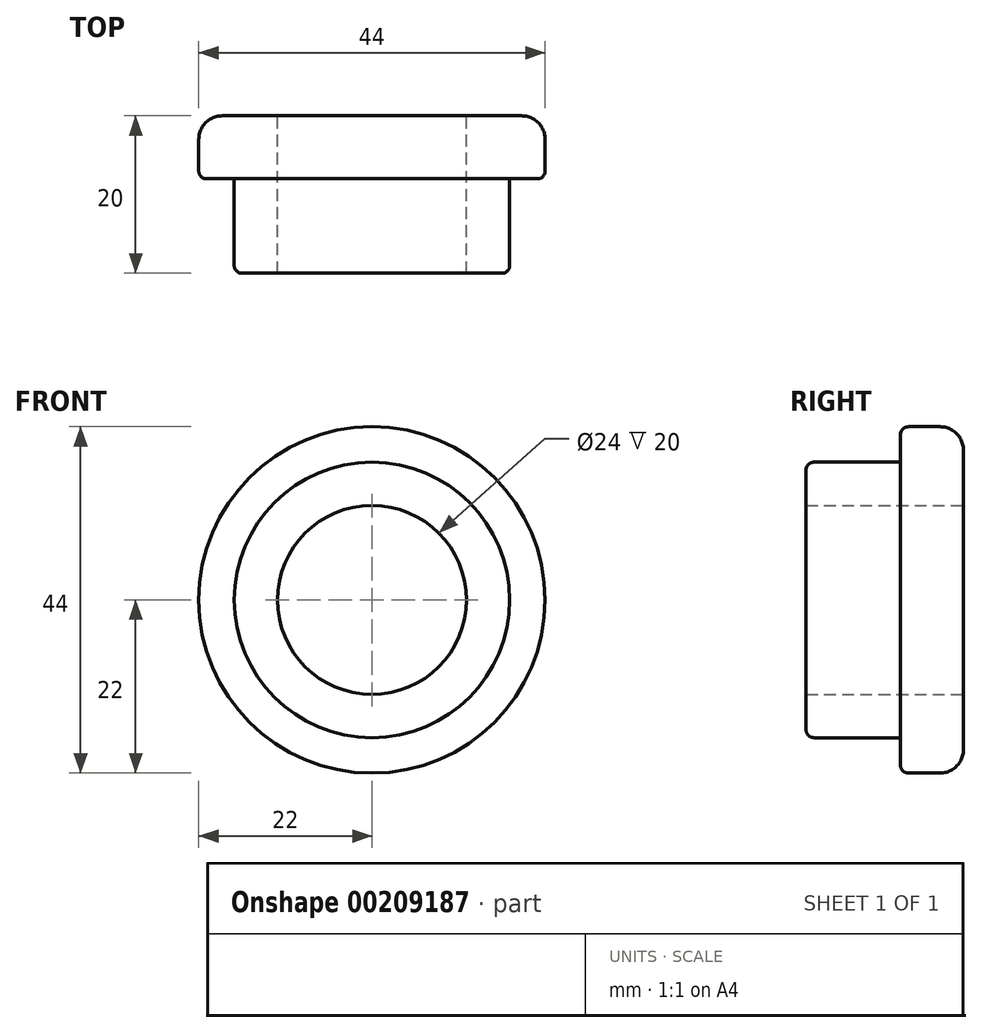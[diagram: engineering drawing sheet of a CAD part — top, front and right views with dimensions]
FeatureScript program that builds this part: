
annotation { "Feature Type Name" : "Feature", "Feature Type Description" : "" }
export const myFeature = defineFeature(function(context is Context, id is Id, definition is map)
    precondition{}
    {
        {
            var Q0;
            Q0=qCreatedBy(makeId("Front.planeOp"),FACE);
            var sketch = newSketch(context, id + "F0", { "sketchPlane" : qUnion([Q0])});
            skCircle(sketch, "E0", {"center": v(0, 0) * mm, "radius": 17.5 * mm});
            skCircle(sketch, "E1", {"center": v(0, 0) * mm, "radius": 22 * mm});
            skCircle(sketch, "E2", {"center": v(0, 0) * mm, "radius": 12 * mm});
            skSolve(sketch);
        }
        {
            var Q0;
            Q0=makeQuery(id+"F0.imprint","IMPRINT",FACE,{"disambiguationData":[TD([[makeQuery(id+"F0.imprint","IMPRINT",EDGE,{"derivedFrom":sQuery(id+"F0.wireOp",EDGE,"E0")}),-1.0]])]});
            var Q1;
            Q1=makeQuery(id+"F0.imprint","IMPRINT",FACE,{"disambiguationData":[TD([[makeQuery(id+"F0.imprint","IMPRINT",EDGE,{"derivedFrom":sQuery(id+"F0.wireOp",EDGE,"E0")}),1.0]])]});
            extrude(context, id + "F1", {"entities" : qUnion([Q0, Q1]), "depth" : 8 * mm});
        }
        {
            var Q0;
            Q0=makeQuery(id+"F0.imprint","IMPRINT",FACE,{"disambiguationData":[TD([[makeQuery(id+"F0.imprint","IMPRINT",EDGE,{"derivedFrom":sQuery(id+"F0.wireOp",EDGE,"E0")}),1.0]])]});
            extrude(context, id + "F2", {"entities" : qUnion([Q0]), "operationType" : NewBodyOperationType.ADD, "depth" : 20 * mm});
        }
        {
            var Q0;
            Q0=makeQuery(id+"F1.opExtrude","CAP_EDGE",EDGE,{"disambiguationData":[OSD([sQuery(id+"F0.wireOp",EDGE,"E1")])],"isStart":true});
            fillet(context, id + "F3", {"entities" : qUnion([Q0]), "radius" : 3 * mm, "tangentPropagation" : true, "allowEdgeOverflow" : false});
        }
        {
            var Q0;
            Q0=makeQuery(id+"F1.opExtrude","CAP_EDGE",EDGE,{"disambiguationData":[OSD([sQuery(id+"F0.wireOp",EDGE,"E1")])],"isStart":false});
            fillet(context, id + "F4", {"entities" : qUnion([Q0]), "radius" : 1 * mm, "tangentPropagation" : true, "allowEdgeOverflow" : false});
        }
        {
            var Q0;
            Q0=makeQuery(id+"F2.opExtrude","CAP_EDGE",EDGE,{"disambiguationData":[OSD([sQuery(id+"F0.wireOp",EDGE,"E0")])],"isStart":false});
            fillet(context, id + "F5", {"entities" : qUnion([Q0]), "radius" : 1 * mm, "tangentPropagation" : true, "allowEdgeOverflow" : false});
        }
    });
